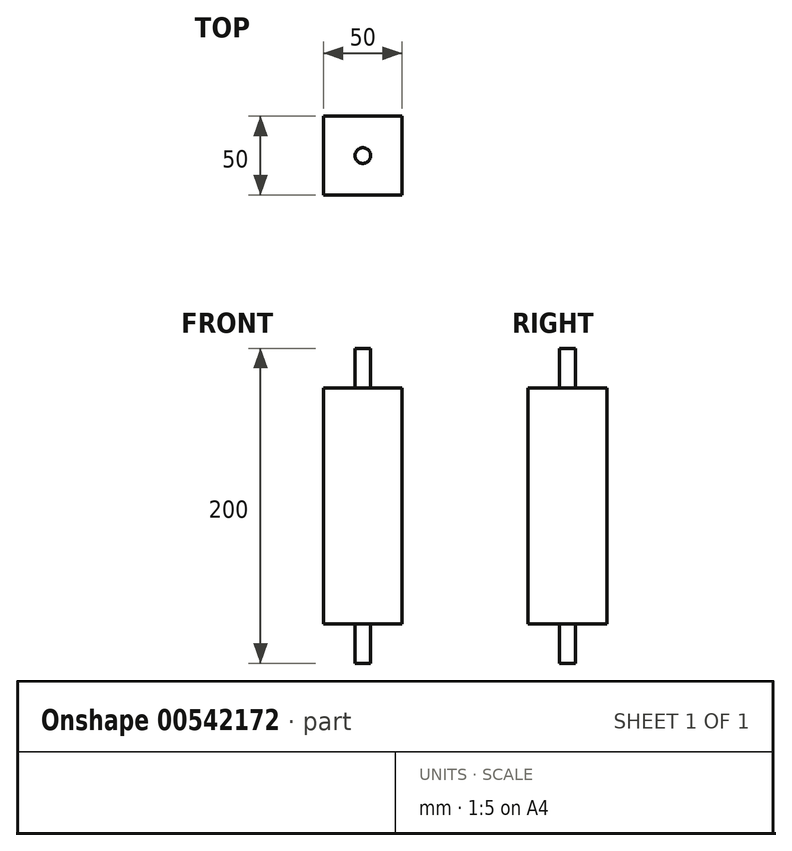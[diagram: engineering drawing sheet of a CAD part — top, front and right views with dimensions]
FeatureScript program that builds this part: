
annotation { "Feature Type Name" : "Feature", "Feature Type Description" : "" }
export const myFeature = defineFeature(function(context is Context, id is Id, definition is map)
    precondition{}
    {
        {
            var Q0;
            Q0=qCreatedBy(makeId("Top.planeOp"),FACE);
            var sketch = newSketch(context, id + "F0", { "sketchPlane" : qUnion([Q0])});
            skLineSegment(sketch, "E0.bottom", {"start": v(25, 25) * mm, "end": v(-25, 25) * mm});
            skLineSegment(sketch, "E0.top", {"start": v(25, -25) * mm, "end": v(-25, -25) * mm});
            skLineSegment(sketch, "E0.left", {"start": v(25, 25) * mm, "end": v(25, -25) * mm});
            skLineSegment(sketch, "E0.right", {"start": v(-25, 25) * mm, "end": v(-25, -25) * mm});
            skPoint(sketch, "E0.middle", {"position": v(0, 0) * mm});
            skSolve(sketch);
        }
        {
            var Q0;
            Q0=makeQuery(id+"F0.imprint","IMPRINT",FACE,{"disambiguationData":[TD([[makeQuery(id+"F0.imprint","IMPRINT",EDGE,{"derivedFrom":sQuery(id+"F0.wireOp",EDGE,"E0.bottom")}),1.0]])]});
            extrude(context, id + "F1", {"entities" : qUnion([Q0]), "endBound" : BoundingType.SYMMETRIC, "depth" : 150 * mm, "offsetDistance" : 25 * mm});
        }
        {
            var Q0;
            Q0=makeQuery(id+"F1.opExtrude","CAP_FACE",FACE,{"disambiguationData":[OSD([sQuery(id+"F0.wireOp",EDGE,"E0.bottom"),sQuery(id+"F0.wireOp",EDGE,"E0.top"),sQuery(id+"F0.wireOp",EDGE,"E0.left"),sQuery(id+"F0.wireOp",EDGE,"E0.right")])],"isStart":true});
            var sketch = newSketch(context, id + "F2", { "sketchPlane" : qUnion([Q0])});
            skCircle(sketch, "E1", {"center": v(0, 0) * mm, "radius": 5 * mm});
            skSolve(sketch);
        }
        {
            var Q0;
            Q0 = qSketchRegion(id + "F2", true);
            extrude(context, id + "F3", {"entities" : qUnion([Q0]), "operationType" : NewBodyOperationType.ADD, "depth" : 25 * mm, "offsetDistance" : 25 * mm});
        }
        {
            var Q0;
            Q0=makeQuery(id+"F1.opExtrude","CAP_FACE",FACE,{"disambiguationData":[OSD([sQuery(id+"F0.wireOp",EDGE,"E0.bottom"),sQuery(id+"F0.wireOp",EDGE,"E0.top"),sQuery(id+"F0.wireOp",EDGE,"E0.left"),sQuery(id+"F0.wireOp",EDGE,"E0.right")])],"isStart":false});
            var sketch = newSketch(context, id + "F4", { "sketchPlane" : qUnion([Q0])});
            skCircle(sketch, "E2", {"center": v(0, 0) * mm, "radius": 5 * mm});
            skSolve(sketch);
        }
        {
            var Q0;
            Q0 = qSketchRegion(id + "F4", true);
            extrude(context, id + "F5", {"entities" : qUnion([Q0]), "operationType" : NewBodyOperationType.ADD, "depth" : 25 * mm, "offsetDistance" : 25 * mm});
        }
    });
